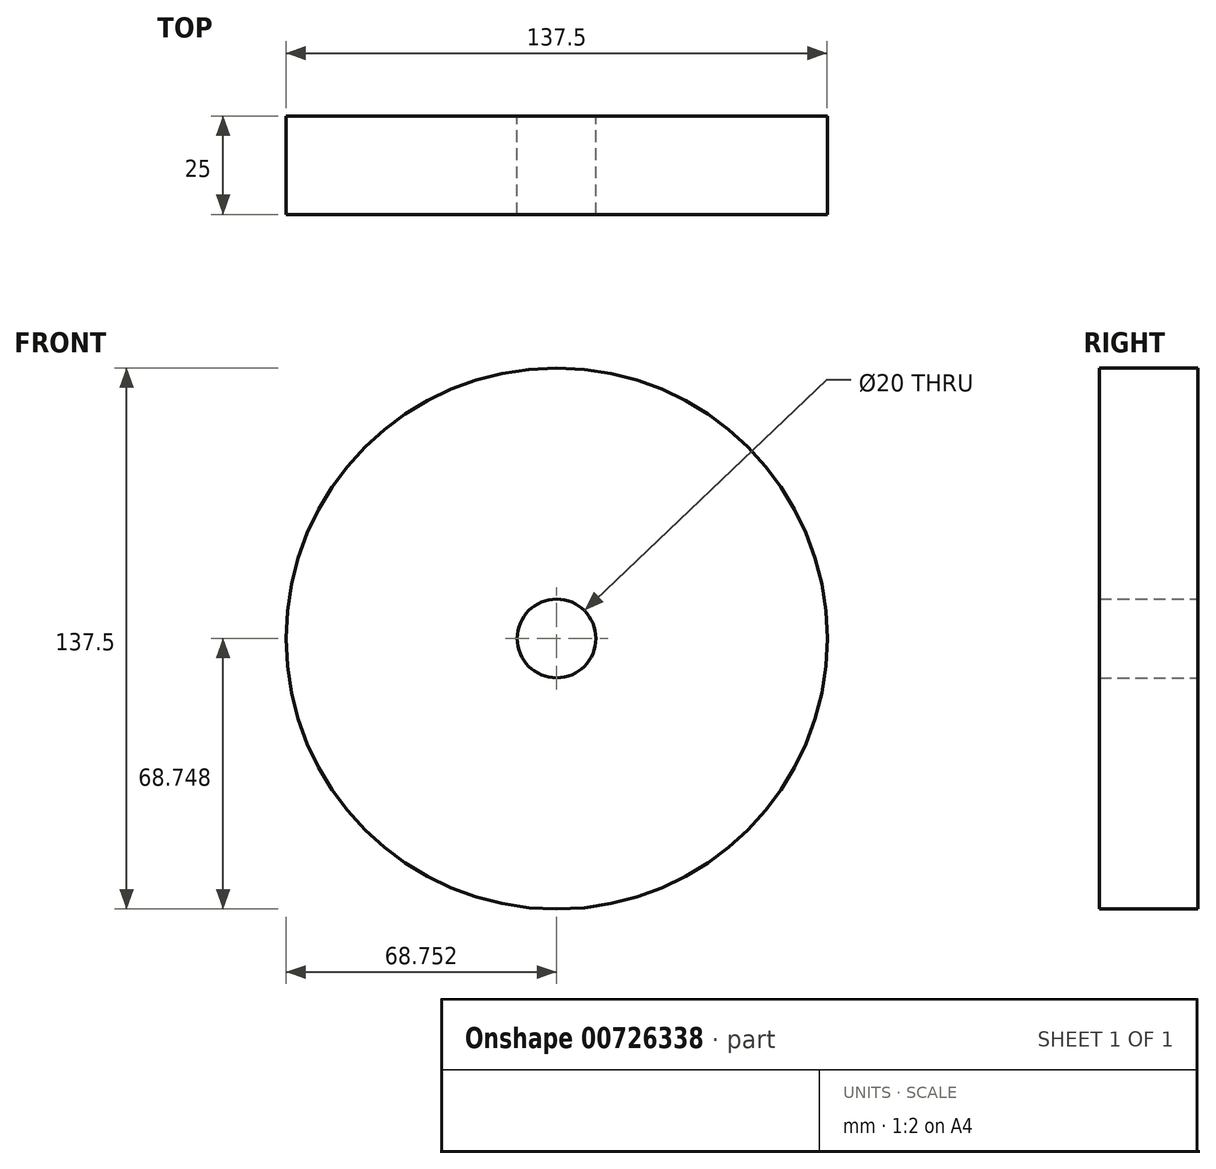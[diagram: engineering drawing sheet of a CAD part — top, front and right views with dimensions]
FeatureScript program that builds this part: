
annotation { "Feature Type Name" : "Feature", "Feature Type Description" : "" }
export const myFeature = defineFeature(function(context is Context, id is Id, definition is map)
    precondition{}
    {
        {
            var Q0;
            Q0=qCreatedBy(makeId("Front.planeOp"),FACE);
            var sketch = newSketch(context, id + "F0", { "sketchPlane" : qUnion([Q0])});
            skCircle(sketch, "E0", {"center": v(-11.96, -7.86) * mm, "radius": 68.75 * mm});
            skCircle(sketch, "E1", {"center": v(-11.96, -7.86) * mm, "radius": 10 * mm});
            skSolve(sketch);
        }
        {
            var Q0;
            Q0 = qSketchRegion(id + "F0", true);
            var Q1;
            Q1=makeQuery(id+"F0.imprint","IMPRINT",FACE,{"disambiguationData":[TD([[makeQuery(id+"F0.imprint","IMPRINT",EDGE,{"derivedFrom":sQuery(id+"F0.wireOp",EDGE,"E0")}),1.0]])]});
            extrude(context, id + "F1", {"entities" : qUnion([Q0, Q1]), "depth" : 25 * mm, "offsetDistance" : 25 * mm});
        }
    });
